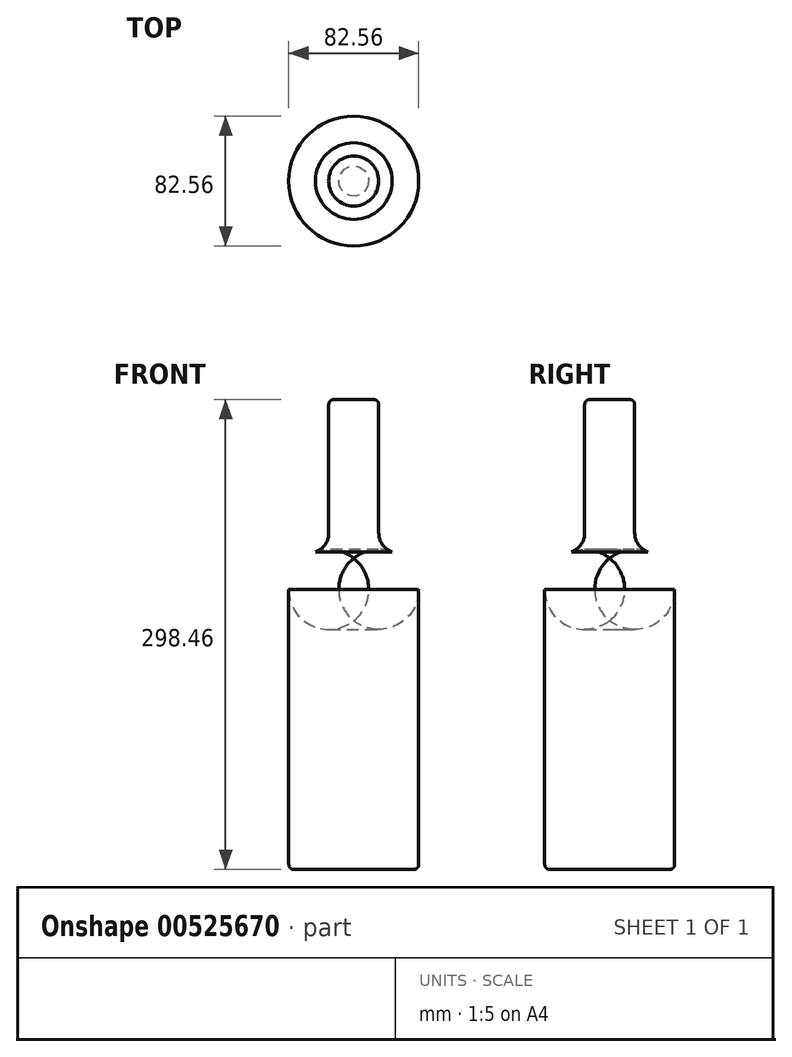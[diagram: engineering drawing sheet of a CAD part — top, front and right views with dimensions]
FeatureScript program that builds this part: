
annotation { "Feature Type Name" : "Feature", "Feature Type Description" : "" }
export const myFeature = defineFeature(function(context is Context, id is Id, definition is map)
    precondition{}
    {
        {
            var Q0;
            Q0=qCreatedBy(makeId("Front.planeOp"),FACE);
            var sketch = newSketch(context, id + "F0", { "sketchPlane" : qUnion([Q0])});
            skLineSegment(sketch, "E0", {"start": v(0, 149.23) * mm, "end": v(0, -149.23) * mm});
            skLineSegment(sketch, "E1", {"start": v(0, -149.23) * mm, "end": v(41.28, -149.23) * mm});
            skLineSegment(sketch, "E2", {"start": v(41.28, -149.23) * mm, "end": v(41.28, 53.98) * mm});
            skLineSegment(sketch, "E3", {"start": v(41.28, 53.97) * mm, "end": v(15.88, 53.97) * mm});
            skLineSegment(sketch, "E4", {"start": v(15.88, 53.97) * mm, "end": v(15.88, 149.23) * mm});
            skLineSegment(sketch, "E5", {"start": v(15.88, 149.23) * mm, "end": v(0, 149.23) * mm});
            skSolve(sketch);
        }
        {
            var Q0;
            Q0=makeQuery(id+"F0.imprint","IMPRINT",FACE,{"disambiguationData":[TD([[makeQuery(id+"F0.imprint","IMPRINT",EDGE,{"derivedFrom":sQuery(id+"F0.wireOp",EDGE,"E0")}),1.0]])]});
            var Q1;
            Q1=sQuery(id+"F0.wireOp",EDGE,"E0");
            revolve(context, id + "F1", {"entities" : qUnion([Q0]), "axis" : qUnion([Q1]), "revolveType" : RevolveType.FULL});
        }
        {
            var Q0;
            Q0=makeQuery(id+"F1.opRevolve","SWEPT_EDGE",EDGE,{"disambiguationData":[OSD([sQuery(id+"F0.wireOp",EDGE,"E2"),sQuery(id+"F0.wireOp",EDGE,"E3")])]});
            fillet(context, id + "F2", {"entities" : qUnion([Q0]), "radius" : 25.4 * mm, "tangentPropagation" : true, "allowEdgeOverflow" : false});
        }
        {
            var Q0;
            Q0=makeQuery(id+"F2.opFillet","BLEND_EDGE",EDGE,{"blendedFrom":[makeQuery(id+"F1.opRevolve","SWEPT_EDGE",EDGE,{"disambiguationData":[OSD([sQuery(id+"F0.wireOp",EDGE,"E2"),sQuery(id+"F0.wireOp",EDGE,"E3")])]}),makeQuery(id+"F1.opRevolve","SWEPT_FACE",FACE,{"disambiguationData":[OSD([sQuery(id+"F0.wireOp",EDGE,"E4")])]})],"blendedInto":[makeQuery(id+"F1.opRevolve","SWEPT_FACE",FACE,{"disambiguationData":[OSD([sQuery(id+"F0.wireOp",EDGE,"E4")])]})]});
            fillet(context, id + "F3", {"entities" : qUnion([Q0]), "radius" : 12.7 * mm, "tangentPropagation" : true, "allowEdgeOverflow" : false});
        }
        {
            var Q0;
            Q0=makeQuery(id+"F1.opRevolve","SWEPT_EDGE",EDGE,{"disambiguationData":[OSD([sQuery(id+"F0.wireOp",EDGE,"E4"),sQuery(id+"F0.wireOp",EDGE,"E5")])]});
            var Q1;
            Q1=makeQuery(id+"F1.opRevolve","SWEPT_EDGE",EDGE,{"disambiguationData":[OSD([sQuery(id+"F0.wireOp",EDGE,"E1"),sQuery(id+"F0.wireOp",EDGE,"E2")])]});
            fillet(context, id + "F4", {"entities" : qUnion([Q0, Q1]), "radius" : 3.17 * mm, "tangentPropagation" : true, "allowEdgeOverflow" : false});
        }
    });
